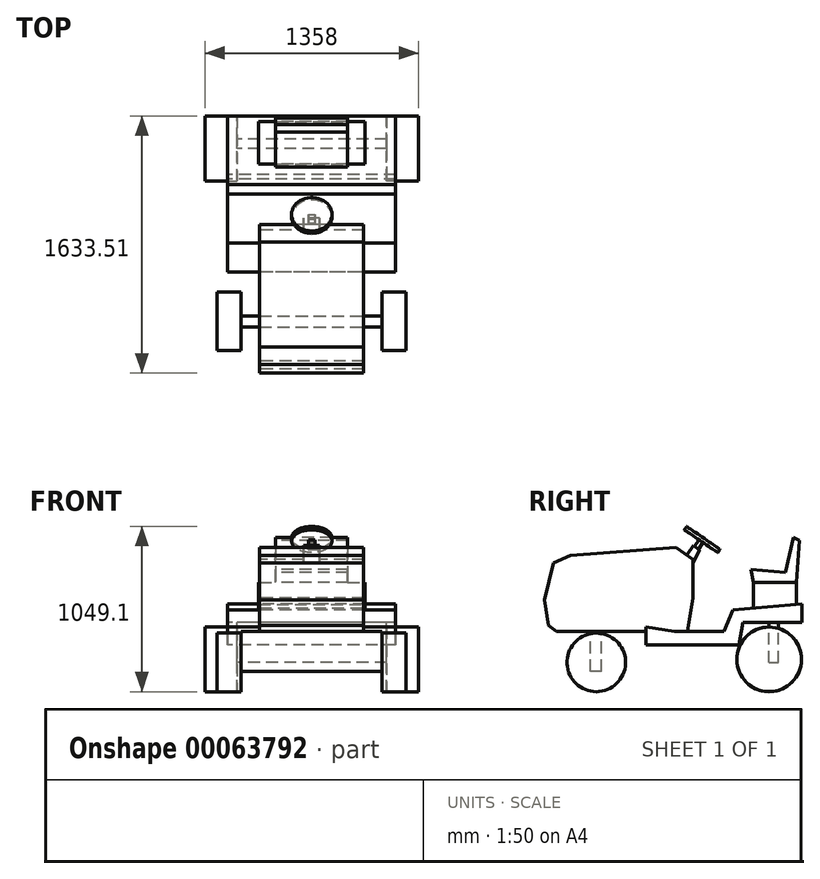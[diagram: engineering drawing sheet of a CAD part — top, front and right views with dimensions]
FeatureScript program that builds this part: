
annotation { "Feature Type Name" : "Feature", "Feature Type Description" : "" }
export const myFeature = defineFeature(function(context is Context, id is Id, definition is map)
    precondition{}
    {
        {
            var Q0;
            Q0=qCreatedBy(makeId("Top.planeOp"),FACE);
            var sketch = newSketch(context, id + "F0", { "sketchPlane" : qUnion([Q0])});
            skLineSegment(sketch, "E0.bottom", {"start": v(-684.79, 956.16) * mm, "end": v(686.81, 956.16) * mm});
            skLineSegment(sketch, "E0.top", {"start": v(-684.79, -771.04) * mm, "end": v(686.81, -771.04) * mm});
            skLineSegment(sketch, "E0.left", {"start": v(-684.79, 956.16) * mm, "end": v(-684.79, -771.04) * mm});
            skLineSegment(sketch, "E0.right", {"start": v(686.81, 956.16) * mm, "end": v(686.81, -771.04) * mm});
            skSolve(sketch);
        }
        {
            var Q0;
            Q0=qCreatedBy(makeId("Right.planeOp"),FACE);
            var sketch = newSketch(context, id + "F1", { "sketchPlane" : qUnion([Q0])});
            skLineSegment(sketch, "E1.bottom", {"start": v(954.63, 0) * mm, "end": v(-771.04, 0) * mm});
            skLineSegment(sketch, "E1.top", {"start": v(954.63, 1041.4) * mm, "end": v(-771.04, 1041.4) * mm});
            skLineSegment(sketch, "E1.left", {"start": v(954.63, 0) * mm, "end": v(954.63, 1041.4) * mm});
            skLineSegment(sketch, "E1.right", {"start": v(-771.04, 0) * mm, "end": v(-771.04, 1041.4) * mm});
            skSolve(sketch);
        }
        {
            var Q0;
            Q0=makeQuery(id+"F1.imprint","IMPRINT",FACE,{"disambiguationData":[TD([[makeQuery(id+"F1.imprint","IMPRINT",EDGE,{"derivedFrom":sQuery(id+"F1.wireOp",EDGE,"E1.bottom")}),-1.0]])]});
            var sketch = newSketch(context, id + "F2", { "sketchPlane" : qUnion([Q0])});
            skLineSegment(sketch, "E2.0", {"start": v(954.63, 438.64) * mm, "end": v(954.63, 557.7) * mm});
            skLineSegment(sketch, "E3", {"start": v(954.63, 557.7) * mm, "end": v(517.3, 520.7) * mm});
            skPoint(sketch, "E3.endSnap0", {"position": v(954.63, 520.7) * mm});
            skLineSegment(sketch, "E4", {"start": v(517.3, 520.7) * mm, "end": v(458.98, 382.76) * mm});
            skLineSegment(sketch, "E5", {"start": v(458.98, 382.76) * mm, "end": v(145.54, 382.76) * mm});
            skLineSegment(sketch, "E6", {"start": v(145.54, 382.76) * mm, "end": v(-36.7, 411.92) * mm});
            skLineSegment(sketch, "E7", {"start": v(-36.7, 411.92) * mm, "end": v(-36.7, 297.72) * mm});
            skLineSegment(sketch, "E8", {"start": v(-36.7, 297.72) * mm, "end": v(553.74, 297.72) * mm});
            skLineSegment(sketch, "E9", {"start": v(553.74, 297.72) * mm, "end": v(580.47, 438.64) * mm});
            skLineSegment(sketch, "E10", {"start": v(580.47, 438.64) * mm, "end": v(954.63, 438.64) * mm});
            skPoint(sketch, "E11.orphan", {"position": v(954.63, 1041.4) * mm});
            skPoint(sketch, "E12.0.end.orphan", {"position": v(-771.04, 1041.4) * mm});
            skPoint(sketch, "E13.0.start.orphan", {"position": v(-771.04, 0) * mm});
            skPoint(sketch, "E14.0.start.orphan", {"position": v(954.63, 0) * mm});
            skSolve(sketch);
        }
        {
            var Q0;
            Q0 = qSketchRegion(id + "F2", true);
            extrude(context, id + "F3", {"entities" : qUnion([Q0]), "endBound" : BoundingType.SYMMETRIC, "depth" : 1066.8 * mm});
        }
        {
            var Q0;
            Q0=makeQuery(id+"F1.imprint","IMPRINT",FACE,{"disambiguationData":[TD([[makeQuery(id+"F1.imprint","IMPRINT",EDGE,{"derivedFrom":sQuery(id+"F1.wireOp",EDGE,"E1.bottom")}),-1.0]])]});
            var sketch = newSketch(context, id + "F4", { "sketchPlane" : qUnion([Q0])});
            skLineSegment(sketch, "E15.0", {"start": v(458.98, 382.76) * mm, "end": v(145.54, 382.76) * mm});
            skLineSegment(sketch, "E16", {"start": v(228.74, 382.76) * mm, "end": v(262.65, 594.7) * mm});
            skLineSegment(sketch, "E17", {"start": v(262.65, 594.7) * mm, "end": v(262.65, 840.83) * mm});
            skLineSegment(sketch, "E18", {"start": v(262.65, 840.83) * mm, "end": v(154.41, 914.7) * mm});
            skLineSegment(sketch, "E19", {"start": v(154.41, 914.7) * mm, "end": v(-513.94, 864.88) * mm});
            skLineSegment(sketch, "E20", {"start": v(-513.94, 864.88) * mm, "end": v(-623.9, 818.5) * mm});
            skLineSegment(sketch, "E21", {"start": v(-623.9, 818.5) * mm, "end": v(-678.88, 583.11) * mm});
            skLineSegment(sketch, "E22", {"start": v(-678.88, 583.11) * mm, "end": v(-653.1, 419.89) * mm});
            skLineSegment(sketch, "E23", {"start": v(228.74, 382.76) * mm, "end": v(-603.28, 382.76) * mm});
            skLineSegment(sketch, "E24", {"start": v(-603.28, 382.76) * mm, "end": v(-653.1, 419.89) * mm});
            skPoint(sketch, "E25.0.end.orphan", {"position": v(553.74, 297.72) * mm});
            skPoint(sketch, "E25.0.start.orphan", {"position": v(-36.7, 297.72) * mm});
            skPoint(sketch, "E26.0.end.orphan", {"position": v(-36.7, 411.92) * mm});
            skSolve(sketch);
        }
        {
            var Q0;
            Q0 = qSketchRegion(id + "F4", true);
            extrude(context, id + "F5", {"entities" : qUnion([Q0]), "operationType" : NewBodyOperationType.ADD, "endBound" : BoundingType.SYMMETRIC, "depth" : 660.4 * mm});
        }
        {
            var Q0;
            Q0=makeQuery(id+"F5.opExtrude","SWEPT_FACE",FACE,{"disambiguationData":[OSD([sQuery(id+"F4.wireOp",EDGE,"E23")])]});
            var sketch = newSketch(context, id + "F6", { "sketchPlane" : qUnion([Q0])});
            skLineSegment(sketch, "E27.rect.bottom", {"start": v(-447.73, 317.68) * mm, "end": v(447.73, 317.68) * mm});
            skLineSegment(sketch, "E27.rect.top", {"start": v(-447.73, 386.72) * mm, "end": v(447.73, 386.72) * mm});
            skLineSegment(sketch, "E27.rect.left", {"start": v(-447.73, 317.68) * mm, "end": v(-447.73, 386.72) * mm});
            skLineSegment(sketch, "E27.rect.right", {"start": v(447.73, 317.68) * mm, "end": v(447.73, 386.72) * mm});
            skPoint(sketch, "E27.rect.middle", {"position": v(0, 352.2) * mm});
            skSolve(sketch);
        }
        {
            var Q0;
            Q0 = qSketchRegion(id + "F6", true);
            extrude(context, id + "F7", {"entities" : qUnion([Q0]), "operationType" : NewBodyOperationType.ADD, "depth" : 254 * mm});
        }
        {
            var Q0;
            Q0=makeQuery(id+"F7.opExtrude","SWEPT_FACE",FACE,{"disambiguationData":[OSD([sQuery(id+"F6.wireOp",EDGE,"E27.rect.left")])]});
            var sketch = newSketch(context, id + "F8", { "sketchPlane" : qUnion([Q0])});
            skLineSegment(sketch, "E28.0", {"start": v(-954.63, 0) * mm, "end": v(771.04, 0) * mm});
            skCircle(sketch, "E29", {"center": v(350.72, 186.22) * mm, "radius": 186.22 * mm});
            skSolve(sketch);
        }
        {
            var Q0;
            Q0 = qSketchRegion(id + "F8", true);
            extrude(context, id + "F9", {"entities" : qUnion([Q0]), "depth" : 152.4 * mm});
        }
        {
            var Q0;
            Q0=makeQuery(id+"F9.opExtrude","SWEPT_BODY",BODY,{"disambiguationData":[OSD([sQuery(id+"F8.wireOp",EDGE,"E29")])]});
            var Q1;
            Q1=makeQuery(id+"F1.imprint","IMPRINT",FACE,{"disambiguationData":[TD([[makeQuery(id+"F1.imprint","IMPRINT",EDGE,{"derivedFrom":sQuery(id+"F1.wireOp",EDGE,"E1.bottom")}),-1.0]])]});
            mirror(context, id + "F10", {"operationType" : NewBodyOperationType.ADD, "entities" : qUnion([Q0]), "mirrorPlane" : qUnion([Q1])});
        }
        {
            var Q0;
            Q0=makeQuery(id+"F3.opExtrude","SWEPT_FACE",FACE,{"disambiguationData":[OSD([sQuery(id+"F2.wireOp",EDGE,"E10")])]});
            var sketch = newSketch(context, id + "F11", { "sketchPlane" : qUnion([Q0])});
            skLineSegment(sketch, "E30.rect.bottom", {"start": v(475.8, -747.09) * mm, "end": v(-475.8, -747.09) * mm});
            skLineSegment(sketch, "E30.rect.top", {"start": v(475.8, -805.5) * mm, "end": v(-475.8, -805.5) * mm});
            skLineSegment(sketch, "E30.rect.left", {"start": v(475.8, -747.09) * mm, "end": v(475.8, -805.5) * mm});
            skLineSegment(sketch, "E30.rect.right", {"start": v(-475.8, -747.09) * mm, "end": v(-475.8, -805.5) * mm});
            skPoint(sketch, "E30.rect.middle", {"position": v(0, -776.3) * mm});
            skPoint(sketch, "E31.orphan", {"position": v(0, -954.63) * mm});
            skSolve(sketch);
        }
        {
            var Q0;
            Q0 = qSketchRegion(id + "F11", true);
            extrude(context, id + "F12", {"entities" : qUnion([Q0]), "operationType" : NewBodyOperationType.ADD, "depth" : 254 * mm});
        }
        {
            var Q0;
            Q0=makeQuery(id+"F12.opExtrude","SWEPT_FACE",FACE,{"disambiguationData":[OSD([sQuery(id+"F11.wireOp",EDGE,"E30.rect.right")])]});
            var sketch = newSketch(context, id + "F13", { "sketchPlane" : qUnion([Q0])});
            skCircle(sketch, "E32", {"center": v(-747.09, 205.12) * mm, "radius": 205.12 * mm});
            skPoint(sketch, "E32.centerSnap0", {"position": v(-747.09, 184.64) * mm});
            skSolve(sketch);
        }
        {
            var Q0;
            Q0 = qSketchRegion(id + "F13", true);
            extrude(context, id + "F14", {"entities" : qUnion([Q0]), "operationType" : NewBodyOperationType.ADD, "depth" : 203.2 * mm});
        }
        {
            var Q0;
            Q0=makeQuery(id+"F12.opExtrude","SWEPT_FACE",FACE,{"disambiguationData":[OSD([sQuery(id+"F11.wireOp",EDGE,"E30.rect.left")])]});
            var sketch = newSketch(context, id + "F15", { "sketchPlane" : qUnion([Q0])});
            skCircle(sketch, "E33", {"center": v(747.09, 205.12) * mm, "radius": 205.12 * mm});
            skArc(sketch, "E34.0", {"start": v(805.5, 401.75) * mm, "mid": v(717.57, 2.13) * mm, "end": v(747.09, 410.25) * mm});
            skSolve(sketch);
        }
        {
            var Q0;
            Q0 = qSketchRegion(id + "F15", true);
            extrude(context, id + "F16", {"entities" : qUnion([Q0]), "operationType" : NewBodyOperationType.ADD, "depth" : 203.2 * mm});
        }
        {
            var Q0;
            Q0=makeQuery(id+"F3.opExtrude","SWEPT_FACE",FACE,{"disambiguationData":[OSD([sQuery(id+"F2.wireOp",EDGE,"E10")])]});
            var sketch = newSketch(context, id + "F17", { "sketchPlane" : qUnion([Q0])});
            skLineSegment(sketch, "E35.rect.bottom", {"start": v(-336.71, -648.84) * mm, "end": v(336.71, -648.84) * mm});
            skLineSegment(sketch, "E35.rect.top", {"start": v(-336.71, -919.68) * mm, "end": v(336.71, -919.68) * mm});
            skLineSegment(sketch, "E35.rect.left", {"start": v(-336.71, -648.84) * mm, "end": v(-336.71, -919.68) * mm});
            skLineSegment(sketch, "E35.rect.right", {"start": v(336.71, -648.84) * mm, "end": v(336.71, -919.68) * mm});
            skPoint(sketch, "E35.rect.middle", {"position": v(0, -784.26) * mm});
            skPoint(sketch, "E35.rect.middle.positionSnap0", {"position": v(0, -747.09) * mm});
            skPoint(sketch, "E35.rect.centerSnap0", {"position": v(0, -747.09) * mm});
            skSolve(sketch);
        }
        {
            var Q0;
            Q0 = qSketchRegion(id + "F17", true);
            extrude(context, id + "F18", {"entities" : qUnion([Q0]), "operationType" : NewBodyOperationType.ADD, "oppositeDirection" : true, "depth" : 254 * mm});
        }
        {
            var Q0;
            Q0=makeQuery(id+"F1.imprint","IMPRINT",FACE,{"disambiguationData":[TD([[makeQuery(id+"F1.imprint","IMPRINT",EDGE,{"derivedFrom":sQuery(id+"F1.wireOp",EDGE,"E1.bottom")}),-1.0]])]});
            var sketch = newSketch(context, id + "F19", { "sketchPlane" : qUnion([Q0])});
            skLineSegment(sketch, "E36.0", {"start": v(648.84, 692.64) * mm, "end": v(919.68, 692.64) * mm});
            skLineSegment(sketch, "E37", {"start": v(919.68, 692.64) * mm, "end": v(939.6, 959.61) * mm});
            skLineSegment(sketch, "E38", {"start": v(939.6, 959.61) * mm, "end": v(900.08, 978.5) * mm});
            skLineSegment(sketch, "E39", {"start": v(900.08, 978.5) * mm, "end": v(850.25, 758.59) * mm});
            skLineSegment(sketch, "E40", {"start": v(850.25, 758.59) * mm, "end": v(630.33, 775.77) * mm});
            skLineSegment(sketch, "E41", {"start": v(630.33, 775.77) * mm, "end": v(648.84, 692.64) * mm});
            skSolve(sketch);
        }
        {
            var Q0;
            Q0 = qSketchRegion(id + "F19", true);
            extrude(context, id + "F20", {"entities" : qUnion([Q0]), "operationType" : NewBodyOperationType.ADD, "endBound" : BoundingType.SYMMETRIC, "depth" : 457.2 * mm});
        }
        {
            var Q0;
            Q0=makeQuery(id+"F1.imprint","IMPRINT",FACE,{"disambiguationData":[TD([[makeQuery(id+"F1.imprint","IMPRINT",EDGE,{"derivedFrom":sQuery(id+"F1.wireOp",EDGE,"E1.bottom")}),-1.0]])]});
            var sketch = newSketch(context, id + "F21", { "sketchPlane" : qUnion([Q0])});
            skLineSegment(sketch, "E42.0", {"start": v(262.65, 840.83) * mm, "end": v(224.07, 867.17) * mm});
            skLineSegment(sketch, "E43.0", {"start": v(262.65, 813.34) * mm, "end": v(262.65, 840.83) * mm});
            skLineSegment(sketch, "E44", {"start": v(224.07, 867.17) * mm, "end": v(265.45, 927.8) * mm});
            skLineSegment(sketch, "E45", {"start": v(265.45, 927.8) * mm, "end": v(304.6, 901.08) * mm});
            skLineSegment(sketch, "E46", {"start": v(304.6, 901.08) * mm, "end": v(262.65, 813.34) * mm});
            skPoint(sketch, "E47.orphan", {"position": v(262.65, 594.7) * mm});
            skPoint(sketch, "E48.orphan", {"position": v(154.41, 914.7) * mm});
            skSolve(sketch);
        }
        {
            var Q0;
            Q0 = qSketchRegion(id + "F21", true);
            extrude(context, id + "F22", {"entities" : qUnion([Q0]), "operationType" : NewBodyOperationType.ADD, "endBound" : BoundingType.SYMMETRIC, "depth" : 101.6 * mm});
        }
        {
            var Q0;
            Q0=makeQuery(id+"F22.opExtrude","SWEPT_FACE",FACE,{"disambiguationData":[OSD([sQuery(id+"F21.wireOp",EDGE,"E45")])]});
            var sketch = newSketch(context, id + "F23", { "sketchPlane" : qUnion([Q0])});
            skLineSegment(sketch, "E49.rect.bottom", {"start": v(-19.95, -294.88) * mm, "end": v(19.95, -294.88) * mm});
            skLineSegment(sketch, "E49.rect.top", {"start": v(-19.95, -262.9) * mm, "end": v(19.95, -262.9) * mm});
            skLineSegment(sketch, "E49.rect.left", {"start": v(-19.95, -294.88) * mm, "end": v(-19.95, -262.9) * mm});
            skLineSegment(sketch, "E49.rect.right", {"start": v(19.95, -294.88) * mm, "end": v(19.95, -262.9) * mm});
            skPoint(sketch, "E49.rect.middle", {"position": v(0, -278.9) * mm});
            skSolve(sketch);
        }
        {
            var Q0;
            Q0 = qSketchRegion(id + "F23", true);
            extrude(context, id + "F24", {"entities" : qUnion([Q0]), "operationType" : NewBodyOperationType.ADD, "depth" : 50.8 * mm});
        }
        {
            var Q0;
            Q0=makeQuery(id+"F24.opExtrude","CAP_FACE",FACE,{"disambiguationData":[OSD([sQuery(id+"F23.wireOp",EDGE,"E49.rect.bottom"),sQuery(id+"F23.wireOp",EDGE,"E49.rect.top"),sQuery(id+"F23.wireOp",EDGE,"E49.rect.left"),sQuery(id+"F23.wireOp",EDGE,"E49.rect.right")])],"isStart":false});
            var sketch = newSketch(context, id + "F25", { "sketchPlane" : qUnion([Q0])});
            skCircle(sketch, "E50", {"center": v(0, -278.9) * mm, "radius": 128.43 * mm});
            skSolve(sketch);
        }
        {
            var Q0;
            Q0 = qSketchRegion(id + "F25", true);
            extrude(context, id + "F26", {"entities" : qUnion([Q0]), "operationType" : NewBodyOperationType.ADD, "depth" : 25.4 * mm});
        }
    });
